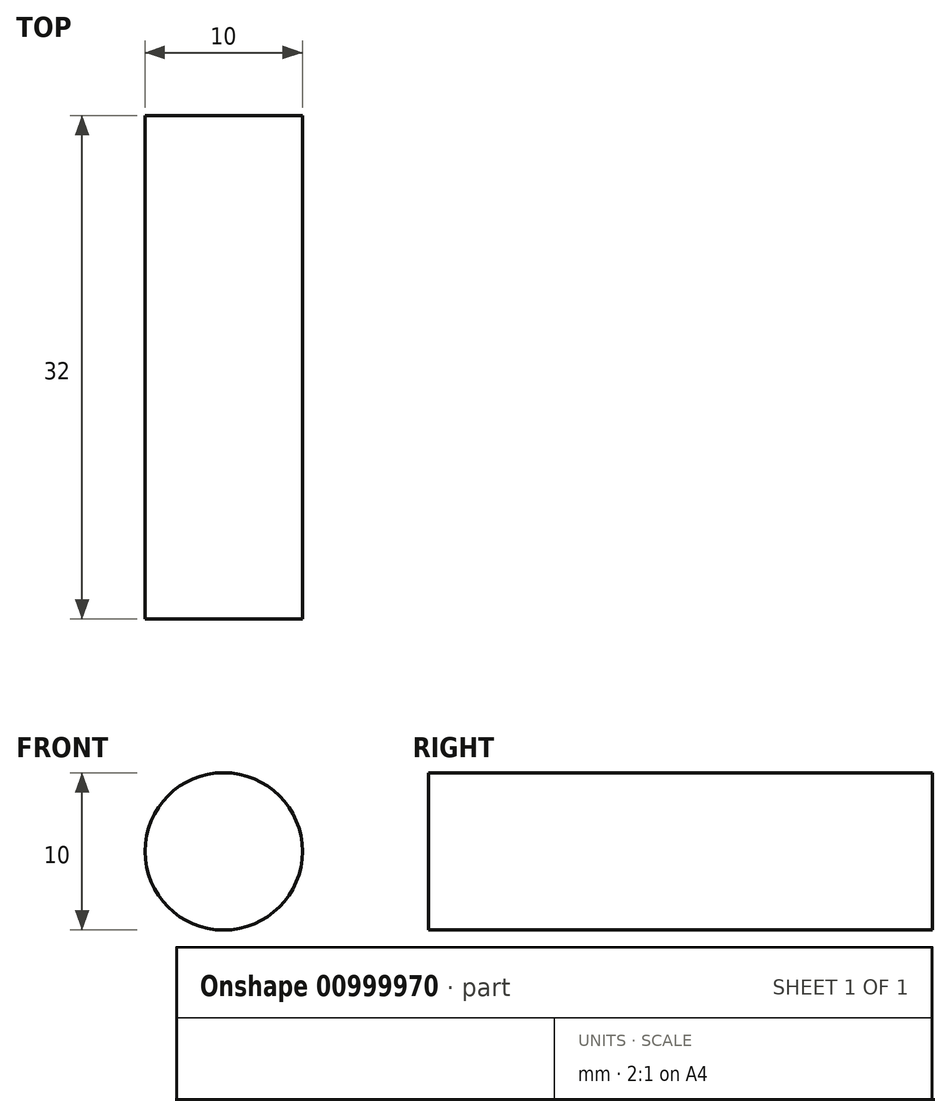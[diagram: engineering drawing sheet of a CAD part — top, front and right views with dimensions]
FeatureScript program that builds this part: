
annotation { "Feature Type Name" : "Feature", "Feature Type Description" : "" }
export const myFeature = defineFeature(function(context is Context, id is Id, definition is map)
    precondition{}
    {
        {
            var Q0;
            Q0=qCreatedBy(makeId("Front.planeOp"),FACE);
            var sketch = newSketch(context, id + "F0", { "sketchPlane" : qUnion([Q0])});
            skCircle(sketch, "E0", {"center": v(0, 0) * mm, "radius": 5 * mm});
            skSolve(sketch);
        }
        {
            var Q0;
            Q0 = qSketchRegion(id + "F0", true);
            extrude(context, id + "F1", {"entities" : qUnion([Q0]), "depth" : 32 * mm, "offsetDistance" : 25 * mm});
        }
    });
